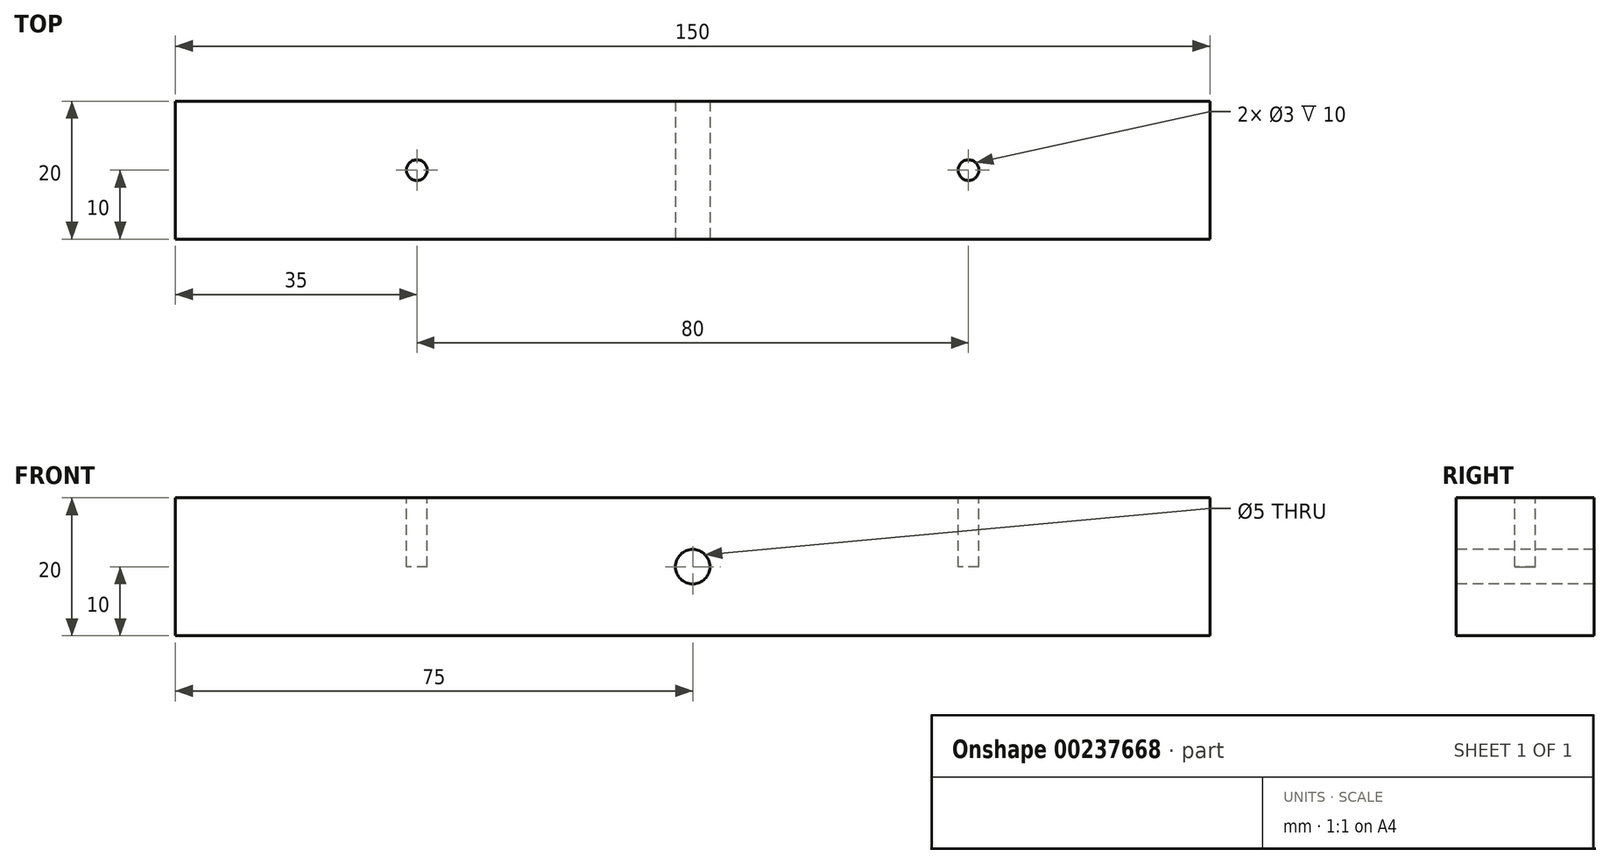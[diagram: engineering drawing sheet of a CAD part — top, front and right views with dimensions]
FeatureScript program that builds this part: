
annotation { "Feature Type Name" : "Feature", "Feature Type Description" : "" }
export const myFeature = defineFeature(function(context is Context, id is Id, definition is map)
    precondition{}
    {
        {
            var Q0;
            Q0=qCreatedBy(makeId("Top.planeOp"),FACE);
            var sketch = newSketch(context, id + "F0", { "sketchPlane" : qUnion([Q0])});
            skLineSegment(sketch, "E0", {"start": v(75, 10) * mm, "end": v(-75, 10) * mm});
            skLineSegment(sketch, "E1", {"start": v(-75, 10) * mm, "end": v(-75, -10) * mm});
            skLineSegment(sketch, "E2", {"start": v(-75, -10) * mm, "end": v(75, -10) * mm});
            skLineSegment(sketch, "E3", {"start": v(75, 10) * mm, "end": v(75, -10) * mm});
            skSolve(sketch);
        }
        {
            var Q0;
            Q0 = qSketchRegion(id + "F0", true);
            extrude(context, id + "F1", {"entities" : qUnion([Q0]), "depth" : 20 * mm});
        }
        {
            var Q0;
            Q0=makeQuery(id+"F1.opExtrude","CAP_FACE",FACE,{"disambiguationData":[OSD([sQuery(id+"F0.wireOp",EDGE,"3V4EPEfO-bZBw-7rHv-MZxK-SMBcoQEjMzqj"),sQuery(id+"F0.wireOp",EDGE,"E0"),sQuery(id+"F0.wireOp",EDGE,"E1"),sQuery(id+"F0.wireOp",EDGE,"E2"),sQuery(id+"F0.wireOp",EDGE,"aciP4cnI-HPXm-VdO5-00Bl-ojwZUDKp0mB4")])],"isStart":false});
            var sketch = newSketch(context, id + "F2", { "sketchPlane" : qUnion([Q0])});
            skCircle(sketch, "E4", {"center": v(40, 0) * mm, "radius": 1.5 * mm});
            skCircle(sketch, "E5", {"center": v(-40, 0) * mm, "radius": 1.5 * mm});
            skSolve(sketch);
        }
        {
            var Q0;
            Q0 = qSketchRegion(id + "F2", true);
            extrude(context, id + "F3", {"entities" : qUnion([Q0]), "operationType" : NewBodyOperationType.REMOVE, "oppositeDirection" : true, "depth" : 10 * mm});
        }
        {
            var Q0;
            Q0=makeQuery(id+"F1.opExtrude","SWEPT_FACE",FACE,{"disambiguationData":[OSD([sQuery(id+"F0.wireOp",EDGE,"E2")])]});
            var sketch = newSketch(context, id + "F4", { "sketchPlane" : qUnion([Q0])});
            skCircle(sketch, "E6", {"center": v(0, 10) * mm, "radius": 2.5 * mm});
            skSolve(sketch);
        }
        {
            var Q0;
            Q0 = qSketchRegion(id + "F4", true);
            extrude(context, id + "F5", {"entities" : qUnion([Q0]), "operationType" : NewBodyOperationType.REMOVE, "oppositeDirection" : true, "depth" : 25 * mm});
        }
    });
